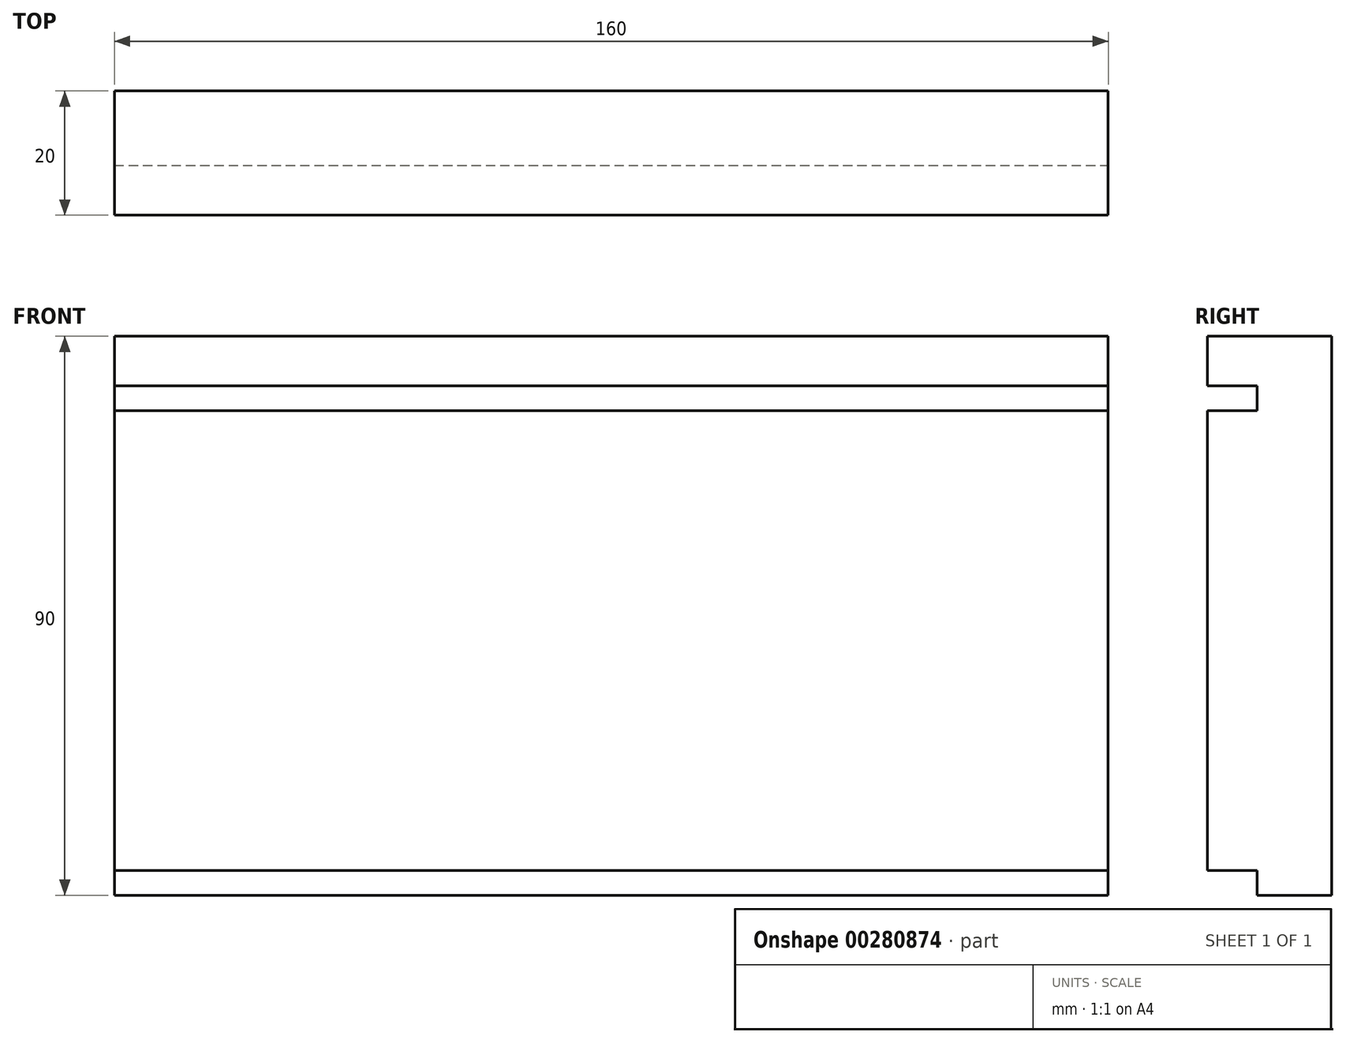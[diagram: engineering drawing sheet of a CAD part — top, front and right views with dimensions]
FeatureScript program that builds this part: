
annotation { "Feature Type Name" : "Feature", "Feature Type Description" : "" }
export const myFeature = defineFeature(function(context is Context, id is Id, definition is map)
    precondition{}
    {
        {
            var Q0;
            Q0=qCreatedBy(makeId("Top.planeOp"),FACE);
            var sketch = newSketch(context, id + "F0", { "sketchPlane" : qUnion([Q0])});
            skLineSegment(sketch, "E0.bottom", {"start": v(-94.71, 6.83) * mm, "end": v(65.29, 6.83) * mm});
            skLineSegment(sketch, "E0.top", {"start": v(-94.71, -13.17) * mm, "end": v(65.29, -13.17) * mm});
            skLineSegment(sketch, "E0.left", {"start": v(-94.71, 6.83) * mm, "end": v(-94.71, -13.17) * mm});
            skLineSegment(sketch, "E0.right", {"start": v(65.29, 6.83) * mm, "end": v(65.29, -13.17) * mm});
            skSolve(sketch);
        }
        {
            var Q0;
            Q0=makeQuery(id+"F0.imprint","IMPRINT",FACE,{"disambiguationData":[TD([[makeQuery(id+"F0.imprint","IMPRINT",EDGE,{"derivedFrom":sQuery(id+"F0.wireOp",EDGE,"E0.bottom")}),-1.0]])]});
            extrude(context, id + "F1", {"entities" : qUnion([Q0]), "depth" : 90 * mm});
        }
        {
            var Q0;
            Q0=makeQuery(id+"F1.opExtrude","SWEPT_FACE",FACE,{"disambiguationData":[OSD([sQuery(id+"F0.wireOp",EDGE,"E0.right")])]});
            var sketch = newSketch(context, id + "F2", { "sketchPlane" : qUnion([Q0])});
            skLineSegment(sketch, "E1.bottom", {"start": v(-13.17, 82) * mm, "end": v(-5.17, 82) * mm});
            skLineSegment(sketch, "E1.top", {"start": v(-13.17, 78) * mm, "end": v(-5.17, 78) * mm});
            skLineSegment(sketch, "E1.left", {"start": v(-13.17, 82) * mm, "end": v(-13.17, 78) * mm});
            skLineSegment(sketch, "E1.right", {"start": v(-5.17, 82) * mm, "end": v(-5.17, 78) * mm});
            skLineSegment(sketch, "E2.bottom", {"start": v(-13.17, 0) * mm, "end": v(-5.17, 0) * mm});
            skLineSegment(sketch, "E2.top", {"start": v(-13.17, 4) * mm, "end": v(-5.17, 4) * mm});
            skLineSegment(sketch, "E2.left", {"start": v(-13.17, 0) * mm, "end": v(-13.17, 4) * mm});
            skLineSegment(sketch, "E2.right", {"start": v(-5.17, 0) * mm, "end": v(-5.17, 4) * mm});
            skSolve(sketch);
        }
        {
            var Q0;
            Q0=makeQuery(id+"F2.imprint","IMPRINT",FACE,{"disambiguationData":[TD([[makeQuery(id+"F2.imprint","IMPRINT",EDGE,{"derivedFrom":sQuery(id+"F2.wireOp",EDGE,"E1.bottom")}),-1.0]])]});
            var Q1;
            Q1=makeQuery(id+"F2.imprint","IMPRINT",FACE,{"disambiguationData":[TD([[makeQuery(id+"F2.imprint","IMPRINT",EDGE,{"derivedFrom":sQuery(id+"F2.wireOp",EDGE,"E2.bottom")}),-1.0]])]});
            extrude(context, id + "F3", {"entities" : qUnion([Q0, Q1]), "operationType" : NewBodyOperationType.REMOVE, "endBound" : BoundingType.UP_TO_NEXT, "oppositeDirection" : true, "depth" : 25 * mm});
        }
    });
